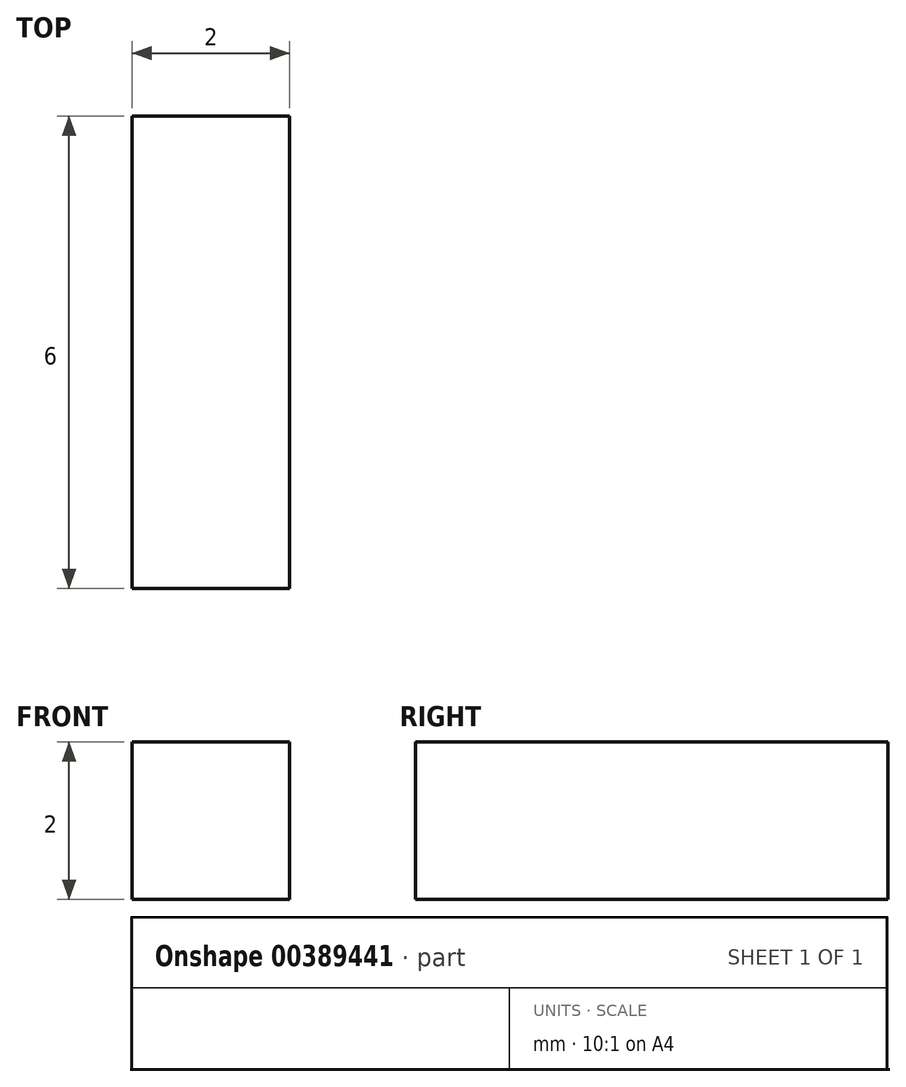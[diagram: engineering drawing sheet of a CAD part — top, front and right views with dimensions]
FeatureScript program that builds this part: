
annotation { "Feature Type Name" : "Feature", "Feature Type Description" : "" }
export const myFeature = defineFeature(function(context is Context, id is Id, definition is map)
    precondition{}
    {
        {
            var Q0;
            Q0=qCreatedBy(makeId("Top.planeOp"),FACE);
            var sketch = newSketch(context, id + "F0", { "sketchPlane" : qUnion([Q0])});
            skLineSegment(sketch, "E0.bottom", {"start": v(1, 3) * mm, "end": v(-1, 3) * mm});
            skLineSegment(sketch, "E0.top", {"start": v(1, -3) * mm, "end": v(-1, -3) * mm});
            skLineSegment(sketch, "E0.left", {"start": v(1, 3) * mm, "end": v(1, -3) * mm});
            skLineSegment(sketch, "E0.right", {"start": v(-1, 3) * mm, "end": v(-1, -3) * mm});
            skPoint(sketch, "E0.middle", {"position": v(0, 0) * mm});
            skSolve(sketch);
        }
        {
            var Q0;
            Q0=qSketchRegion(id+"F0",true);
            extrude(context, id + "F1", {"entities" : qUnion([Q0]), "depth" : 2 * mm});
        }
    });
